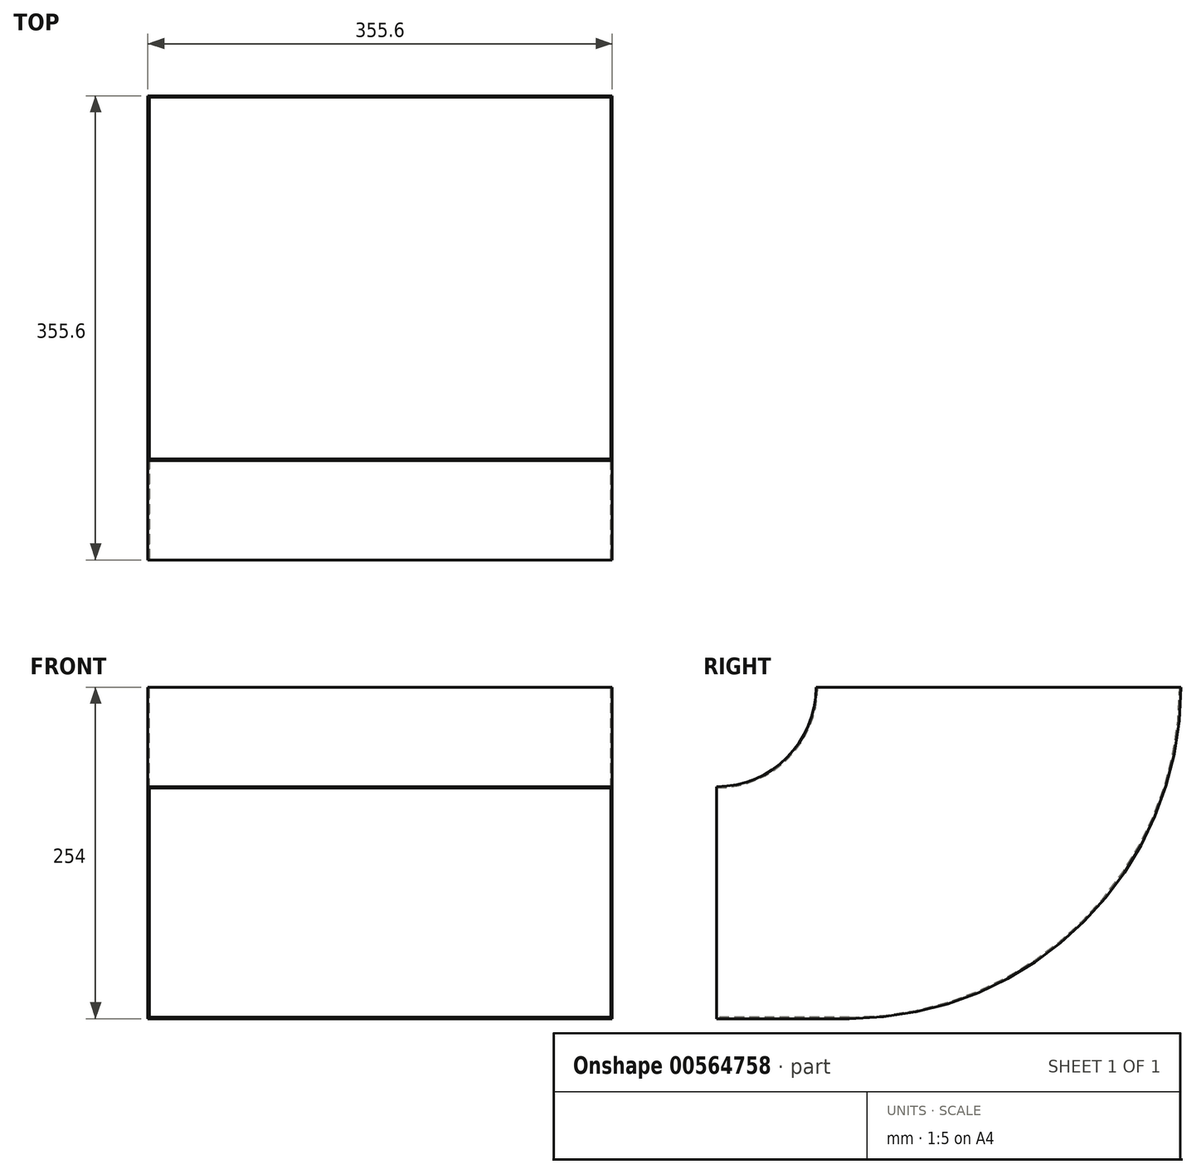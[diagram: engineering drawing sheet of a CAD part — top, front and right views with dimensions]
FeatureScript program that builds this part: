
annotation { "Feature Type Name" : "Feature", "Feature Type Description" : "" }
export const myFeature = defineFeature(function(context is Context, id is Id, definition is map)
    precondition{}
    {
        {
            var Q0;
            Q0=qCreatedBy(makeId("Right.planeOp"),FACE);
            var sketch = newSketch(context, id + "F0", { "sketchPlane" : qUnion([Q0])});
            skArc(sketch, "E0", {"start": v(-76.2, -76.2) * mm, "mid": v(-22.32, -53.88) * mm, "end": v(0, 0) * mm});
            skLineSegment(sketch, "E1", {"start": v(-76.2, -254) * mm, "end": v(-76.2, -76.2) * mm});
            skLineSegment(sketch, "E2", {"start": v(25.4, -254) * mm, "end": v(-76.2, -254) * mm});
            skArc(sketch, "E3", {"start": v(25.4, -254) * mm, "mid": v(205, -179.6) * mm, "end": v(279.4, 0) * mm});
            skLineSegment(sketch, "E4", {"start": v(279.4, 0) * mm, "end": v(0, 0) * mm});
            skSolve(sketch);
        }
        {
            var Q0;
            Q0=makeQuery(id+"F0.imprint","IMPRINT",FACE,{"disambiguationData":[TD([[makeQuery(id+"F0.imprint","IMPRINT",EDGE,{"derivedFrom":sQuery(id+"F0.wireOp",EDGE,"E0")}),-1.0]])]});
            extrude(context, id + "F1", {"entities" : qUnion([Q0]), "depth" : 355.6 * mm, "offsetDistance" : 25.4 * mm});
        }
        {
            var Q0;
            Q0=makeQuery(id+"F1.opExtrude","SWEPT_FACE",FACE,{"disambiguationData":[OSD([sQuery(id+"F0.wireOp",EDGE,"E4")])]});
            var Q1;
            Q1=makeQuery(id+"F1.opExtrude","SWEPT_FACE",FACE,{"disambiguationData":[OSD([sQuery(id+"F0.wireOp",EDGE,"E1")])]});
            shell(context, id + "F2", {"entities" : qUnion([Q0, Q1]), "thickness" : 1.12 * mm});
        }
    });
